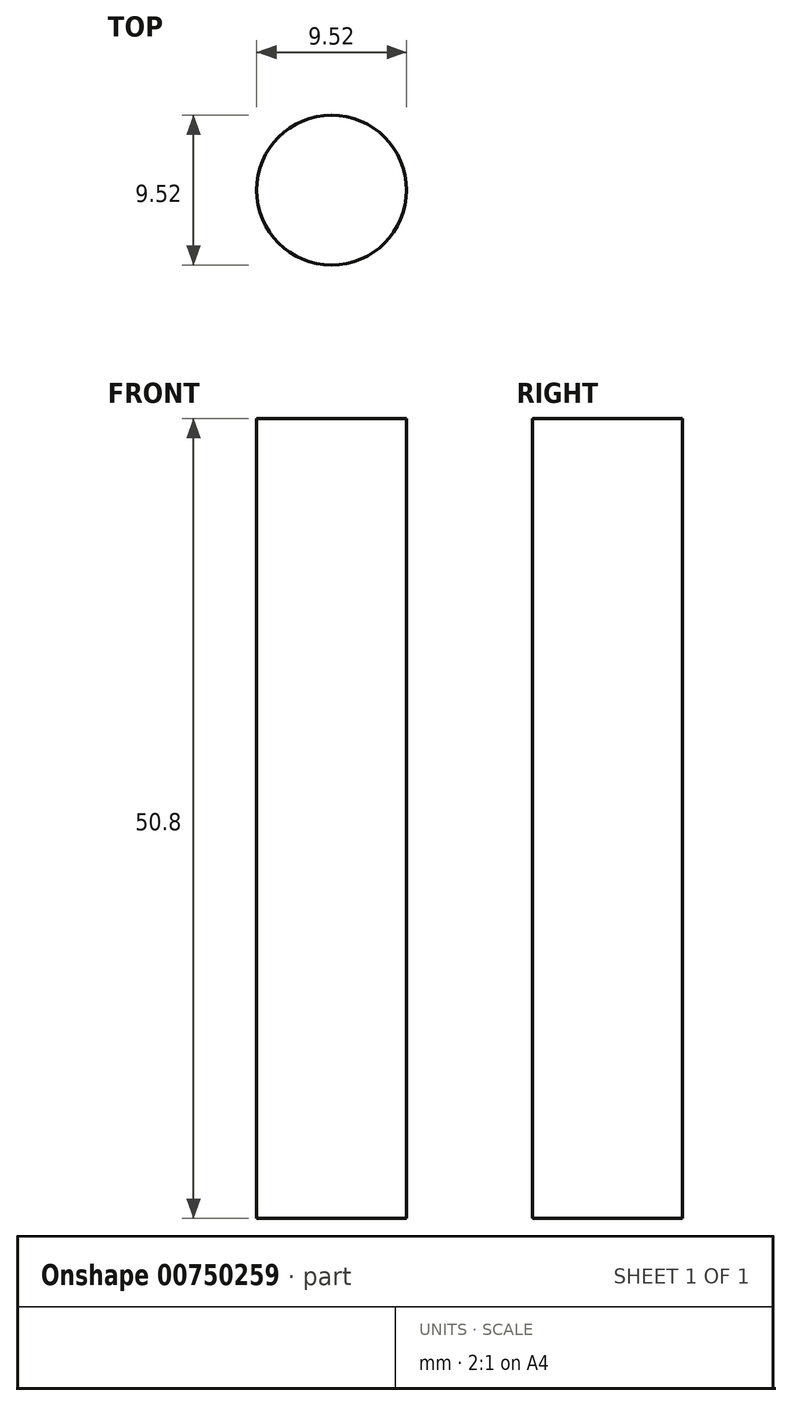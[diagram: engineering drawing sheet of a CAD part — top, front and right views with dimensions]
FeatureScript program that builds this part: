
annotation { "Feature Type Name" : "Feature", "Feature Type Description" : "" }
export const myFeature = defineFeature(function(context is Context, id is Id, definition is map)
    precondition{}
    {
        {
            var Q0;
            Q0=qCreatedBy(makeId("Top.planeOp"),FACE);
            var sketch = newSketch(context, id + "F0", { "sketchPlane" : qUnion([Q0])});
            skCircle(sketch, "E0", {"center": v(0, 0) * mm, "radius": 4.76 * mm});
            skSolve(sketch);
        }
        {
            var Q0;
            Q0=makeQuery(id+"F0.imprint","IMPRINT",FACE,{"disambiguationData":[TD([[makeQuery(id+"F0.imprint","IMPRINT",EDGE,{"derivedFrom":sQuery(id+"F0.wireOp",EDGE,"E0")}),1.0]])]});
            extrude(context, id + "F1", {"entities" : qUnion([Q0]), "depth" : 50.8 * mm, "offsetDistance" : 25.4 * mm});
        }
    });
